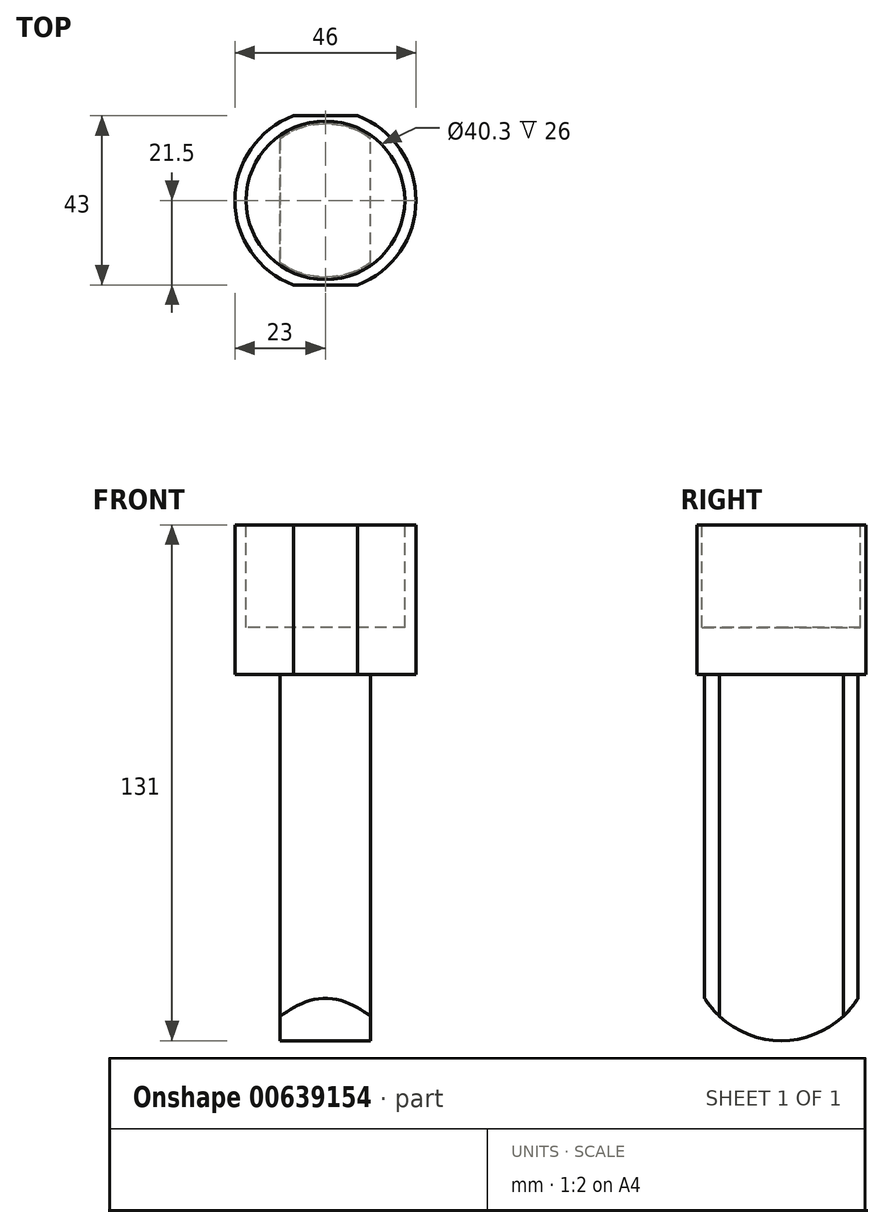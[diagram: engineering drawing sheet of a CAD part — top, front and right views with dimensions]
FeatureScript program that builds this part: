
annotation { "Feature Type Name" : "Feature", "Feature Type Description" : "" }
export const myFeature = defineFeature(function(context is Context, id is Id, definition is map)
    precondition{}
    {
        {
            var Q0;
            Q0=qCreatedBy(makeId("Top.planeOp"),FACE);
            var sketch = newSketch(context, id + "F0", { "sketchPlane" : qUnion([Q0])});
            skArc(sketch, "E0", {"start": v(-8.17, 21.5) * mm, "mid": v(-23, 0) * mm, "end": v(-8.17, -21.5) * mm});
            skLineSegment(sketch, "E1", {"start": v(-8.17, 21.5) * mm, "end": v(8.17, 21.5) * mm});
            skLineSegment(sketch, "E2.MirrorCS", {"start": v(-8.17, -21.5) * mm, "end": v(8.17, -21.5) * mm});
            skArc(sketch, "E3.trimOffspring", {"start": v(8.17, -21.5) * mm, "mid": v(23, 0) * mm, "end": v(8.17, 21.5) * mm});
            skSolve(sketch);
        }
        {
            var Q0;
            Q0=makeQuery(id+"F0.imprint","IMPRINT",FACE,{"disambiguationData":[TD([[makeQuery(id+"F0.imprint","IMPRINT",EDGE,{"derivedFrom":sQuery(id+"F0.wireOp",EDGE,"E0")}),1.0]])]});
            extrude(context, id + "F1", {"entities" : qUnion([Q0]), "depth" : 38 * mm, "offsetDistance" : 25 * mm});
        }
        {
            var Q0;
            Q0=makeQuery(id+"F1.opExtrude","CAP_FACE",FACE,{"disambiguationData":[OSD([sQuery(id+"F0.wireOp",EDGE,"E0"),sQuery(id+"F0.wireOp",EDGE,"E1"),sQuery(id+"F0.wireOp",EDGE,"E2.MirrorCS"),sQuery(id+"F0.wireOp",EDGE,"E3.trimOffspring")])],"isStart":false});
            var sketch = newSketch(context, id + "F2", { "sketchPlane" : qUnion([Q0])});
            skCircle(sketch, "E4", {"center": v(0, 0) * mm, "radius": 20.15 * mm});
            skSolve(sketch);
        }
        {
            var Q0;
            Q0=makeQuery(id+"F2.imprint","IMPRINT",FACE,{"disambiguationData":[TD([[makeQuery(id+"F2.imprint","IMPRINT",EDGE,{"derivedFrom":sQuery(id+"F2.wireOp",EDGE,"E4")}),1.0]])]});
            extrude(context, id + "F3", {"entities" : qUnion([Q0]), "operationType" : NewBodyOperationType.REMOVE, "oppositeDirection" : true, "depth" : 26 * mm, "offsetDistance" : 25 * mm});
        }
        {
            var Q0;
            Q0=makeQuery(id+"F1.opExtrude","CAP_FACE",FACE,{"disambiguationData":[OSD([sQuery(id+"F0.wireOp",EDGE,"E0"),sQuery(id+"F0.wireOp",EDGE,"E1"),sQuery(id+"F0.wireOp",EDGE,"E2.MirrorCS"),sQuery(id+"F0.wireOp",EDGE,"E3.trimOffspring")])],"isStart":true});
            var sketch = newSketch(context, id + "F4", { "sketchPlane" : qUnion([Q0])});
            skArc(sketch, "E5", {"start": v(-11.5, -15.75) * mm, "mid": v(0, -19.5) * mm, "end": v(11.5, -15.75) * mm});
            skLineSegment(sketch, "E6", {"start": v(-11.5, 15.75) * mm, "end": v(-11.5, -15.75) * mm});
            skLineSegment(sketch, "E7.MirrorCS", {"start": v(11.5, 15.75) * mm, "end": v(11.5, -15.75) * mm});
            skArc(sketch, "E8.trimOffspring", {"start": v(11.5, 15.75) * mm, "mid": v(0, 19.5) * mm, "end": v(-11.5, 15.75) * mm});
            skSolve(sketch);
        }
        {
            var Q0;
            Q0=makeQuery(id+"F4.imprint","IMPRINT",FACE,{"disambiguationData":[TD([[makeQuery(id+"F4.imprint","IMPRINT",EDGE,{"derivedFrom":sQuery(id+"F4.wireOp",EDGE,"E5")}),1.0]])]});
            extrude(context, id + "F5", {"entities" : qUnion([Q0]), "operationType" : NewBodyOperationType.ADD, "depth" : 93 * mm, "offsetDistance" : 25 * mm});
        }
        {
            var Q0;
            Q0=makeQuery(id+"F5.opExtrude","SWEPT_FACE",FACE,{"disambiguationData":[OSD([sQuery(id+"F4.wireOp",EDGE,"E6")])]});
            var sketch = newSketch(context, id + "F6", { "sketchPlane" : qUnion([Q0])});
            skArc(sketch, "E9", {"start": v(-22.97, -71.08) * mm, "mid": v(-1.21, -92.97) * mm, "end": v(22.73, -73.49) * mm});
            skLineSegment(sketch, "E10", {"start": v(-22.97, -71.08) * mm, "end": v(-36.09, -107.7) * mm});
            skLineSegment(sketch, "E11", {"start": v(-36.09, -107.7) * mm, "end": v(35.2, -105.78) * mm});
            skLineSegment(sketch, "E12", {"start": v(35.2, -105.78) * mm, "end": v(22.73, -73.49) * mm});
            skSolve(sketch);
        }
        {
            var Q0;
            {var subQ0=sQuery(id+"F6.wireOp",EDGE,"E9");var subQ1=sQuery(id+"F4.wireOp",EDGE,"E6");var subQ4=makeQuery(id+"F5.opExtrude","CAP_EDGE",EDGE,{"disambiguationData":[OSD([subQ1])],"isStart":false});var subQ5=makeQuery(id+"F6.imprint","INTERSECT",VERTEX,{"derivedFrom":[subQ4,subQ0]});Q0=makeQuery(id+"F6.imprint","IMPRINT",FACE,{"disambiguationData":[TD([[makeQuery(id+"F6.imprint","IMPRINT",EDGE,{"disambiguationData":[TD([[subQ5,1.0]])],"derivedFrom":subQ0}),-1.0]])]});}
            var Q1;
            {var subQ0=sQuery(id+"F6.wireOp",EDGE,"E9");var subQ1=sQuery(id+"F4.wireOp",EDGE,"E6");var subQ4=makeQuery(id+"F5.opExtrude","CAP_EDGE",EDGE,{"disambiguationData":[OSD([subQ1])],"isStart":false});var subQ5=makeQuery(id+"F6.imprint","INTERSECT",VERTEX,{"derivedFrom":[subQ4,subQ0]});Q1=makeQuery(id+"F6.imprint","IMPRINT",FACE,{"disambiguationData":[TD([[makeQuery(id+"F6.imprint","IMPRINT",EDGE,{"disambiguationData":[TD([[subQ5,-1.0]])],"derivedFrom":subQ0}),-1.0]])]});}
            var Q2;
            {var subQ0=sQuery(id+"F6.wireOp",EDGE,"E10");Q2=makeQuery(id+"F6.imprint","IMPRINT",FACE,{"disambiguationData":[TD([[makeQuery(id+"F6.imprint","IMPRINT",EDGE,{"derivedFrom":subQ0}),1.0]])]});}
            extrude(context, id + "F7", {"entities" : qUnion([Q0, Q1, Q2]), "operationType" : NewBodyOperationType.REMOVE, "endBound" : BoundingType.THROUGH_ALL, "oppositeDirection" : true, "depth" : 25 * mm, "offsetDistance" : 25 * mm});
        }
    });
